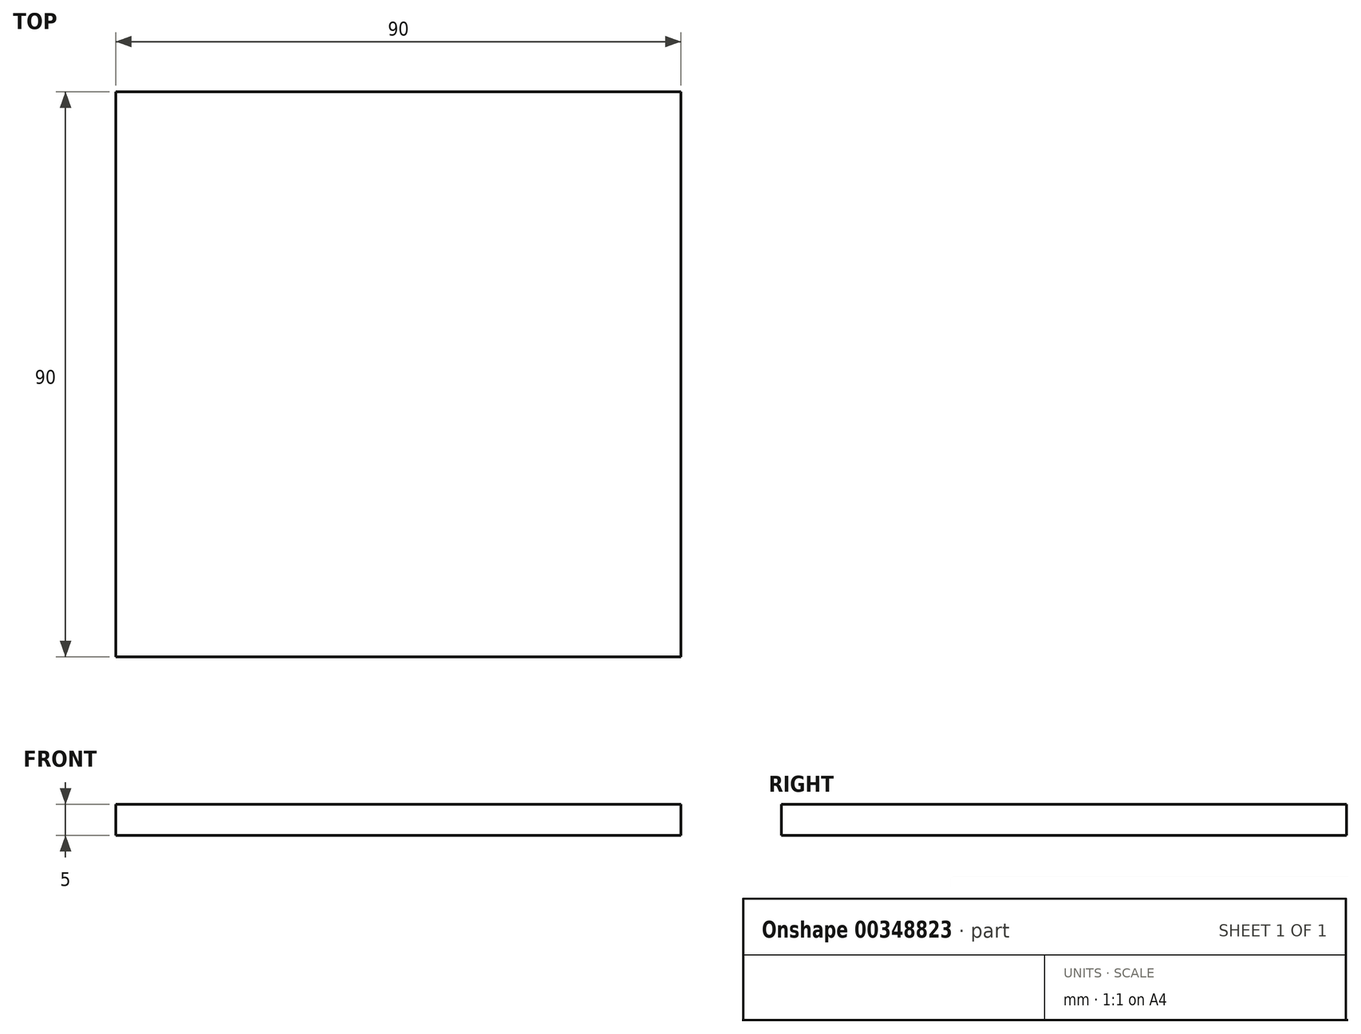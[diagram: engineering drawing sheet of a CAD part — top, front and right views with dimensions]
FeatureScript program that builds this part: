
annotation { "Feature Type Name" : "Feature", "Feature Type Description" : "" }
export const myFeature = defineFeature(function(context is Context, id is Id, definition is map)
    precondition{}
    {
        {
            var Q0;
            Q0=qCreatedBy(makeId("Top.planeOp"),FACE);
            var sketch = newSketch(context, id + "F0", { "sketchPlane" : qUnion([Q0])});
            skLineSegment(sketch, "E0.bottom", {"start": v(-45, 45) * mm, "end": v(45, 45) * mm});
            skLineSegment(sketch, "E0.top", {"start": v(-45, -45) * mm, "end": v(45, -45) * mm});
            skLineSegment(sketch, "E0.left", {"start": v(-45, 45) * mm, "end": v(-45, -45) * mm});
            skLineSegment(sketch, "E0.right", {"start": v(45, 45) * mm, "end": v(45, -45) * mm});
            skSolve(sketch);
        }
        {
            var Q0;
            Q0=makeQuery(id+"F0.imprint","IMPRINT",FACE,{"disambiguationData":[TD([[makeQuery(id+"F0.imprint","IMPRINT",EDGE,{"derivedFrom":sQuery(id+"F0.wireOp",EDGE,"E0.bottom")}),-1.0]])]});
            extrude(context, id + "F1", {"entities" : qUnion([Q0]), "depth" : 5 * mm});
        }
    });
